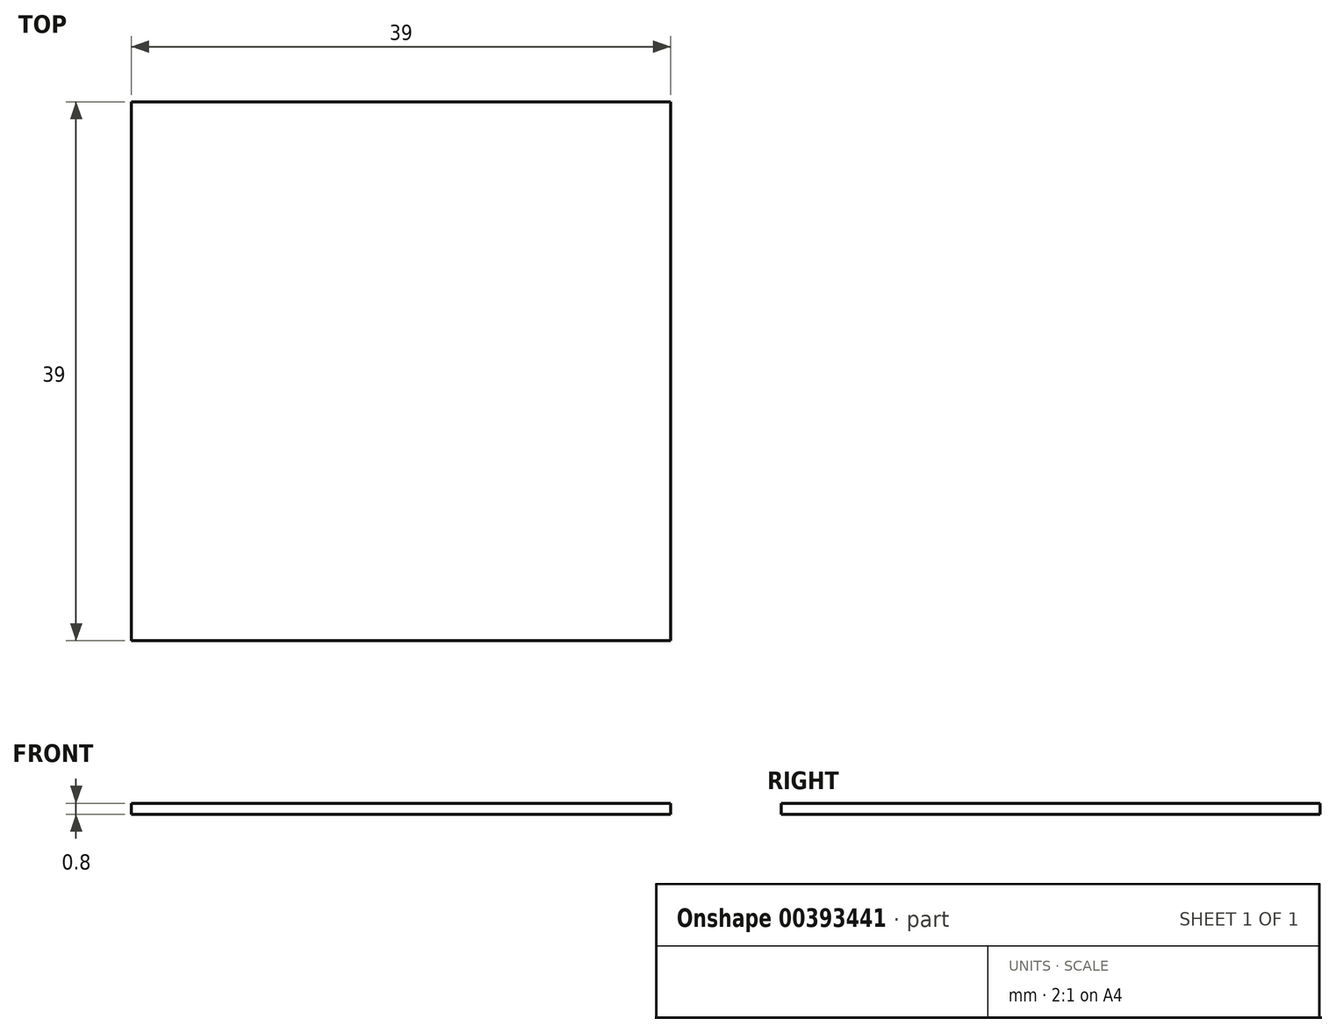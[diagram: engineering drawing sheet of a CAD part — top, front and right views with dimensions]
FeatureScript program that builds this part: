
annotation { "Feature Type Name" : "Feature", "Feature Type Description" : "" }
export const myFeature = defineFeature(function(context is Context, id is Id, definition is map)
    precondition{}
    {
        {
            var Q0;
            Q0=qCreatedBy(makeId("Top.planeOp"),FACE);
            var sketch = newSketch(context, id + "F0", { "sketchPlane" : qUnion([Q0])});
            skLineSegment(sketch, "E0.bottom", {"start": v(-18.74, 23.46) * mm, "end": v(20.26, 23.46) * mm});
            skLineSegment(sketch, "E0.top", {"start": v(-18.74, -15.54) * mm, "end": v(20.26, -15.54) * mm});
            skLineSegment(sketch, "E0.left", {"start": v(-18.74, 23.46) * mm, "end": v(-18.74, -15.54) * mm});
            skLineSegment(sketch, "E0.right", {"start": v(20.26, 23.46) * mm, "end": v(20.26, -15.54) * mm});
            skSolve(sketch);
        }
        {
            var Q0;
            Q0 = qSketchRegion(id + "F0", true);
            extrude(context, id + "F1", {"entities" : qUnion([Q0]), "depth" : .8 * mm});
        }
    });
